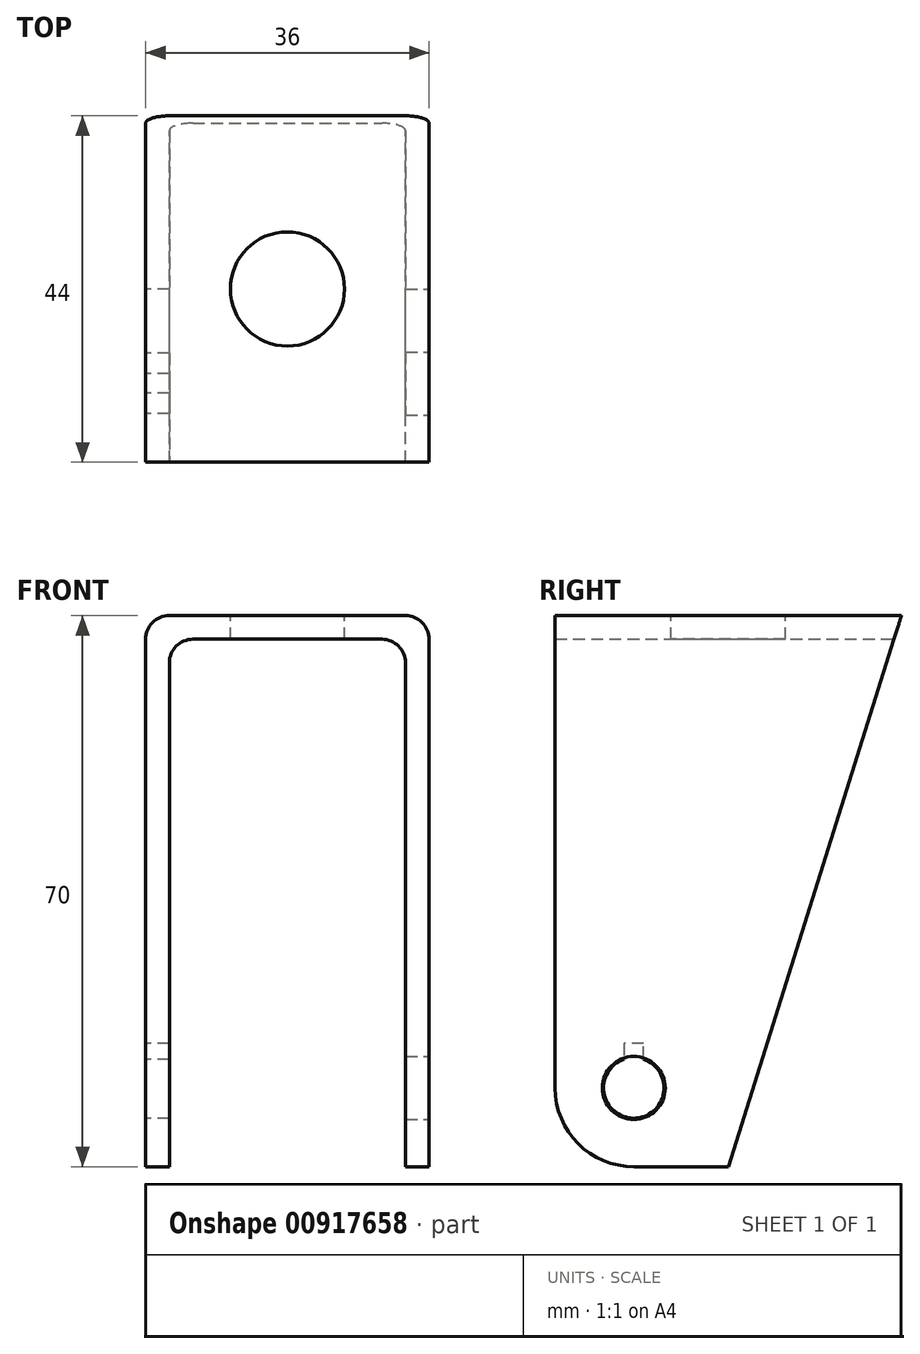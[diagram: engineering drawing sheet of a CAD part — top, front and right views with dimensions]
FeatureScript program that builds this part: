
annotation { "Feature Type Name" : "Feature", "Feature Type Description" : "" }
export const myFeature = defineFeature(function(context is Context, id is Id, definition is map)
    precondition{}
    {
        {
            var Q0;
            Q0=qCreatedBy(makeId("Front.planeOp"),FACE);
            var sketch = newSketch(context, id + "F0", { "sketchPlane" : qUnion([Q0])});
            skLineSegment(sketch, "E0", {"start": v(0, 0) * mm, "end": v(0, 70) * mm});
            skLineSegment(sketch, "E1", {"start": v(0, 70) * mm, "end": v(36, 70) * mm});
            skLineSegment(sketch, "E2", {"start": v(36, 70) * mm, "end": v(36, 0) * mm});
            skLineSegment(sketch, "E3", {"start": v(3, 0) * mm, "end": v(3, 67) * mm});
            skLineSegment(sketch, "E4", {"start": v(3, 67) * mm, "end": v(33, 67) * mm});
            skLineSegment(sketch, "E5", {"start": v(33, 67) * mm, "end": v(33, 0) * mm});
            skLineSegment(sketch, "E6", {"start": v(0, 0) * mm, "end": v(3, 0) * mm});
            skLineSegment(sketch, "E7", {"start": v(33, 0) * mm, "end": v(36, 0) * mm});
            skSolve(sketch);
        }
        {
            var Q0;
            Q0 = qSketchRegion(id + "F0", true);
            extrude(context, id + "F1", {"entities" : qUnion([Q0]), "depth" : 44 * mm, "offsetDistance" : 25 * mm});
        }
        {
            var Q0;
            Q0=makeQuery(id+"F1.opExtrude","SWEPT_FACE",FACE,{"disambiguationData":[OSD([sQuery(id+"F0.wireOp",EDGE,"E2")])]});
            var sketch = newSketch(context, id + "F2", { "sketchPlane" : qUnion([Q0])});
            skCircle(sketch, "E8", {"center": v(-34, 10) * mm, "radius": 4 * mm});
            skLineSegment(sketch, "E9", {"start": v(0, 70) * mm, "end": v(-22, 0) * mm});
            skSolve(sketch);
        }
        {
            var Q0;
            Q0=makeQuery(id+"F2.imprint","IMPRINT",FACE,{"disambiguationData":[TD([[makeQuery(id+"F2.imprint","IMPRINT",EDGE,{"derivedFrom":sQuery(id+"F2.wireOp",EDGE,"E8")}),1.0]])]});
            var Q1;
            {var subQ0=sQuery(id+"F2.wireOp",EDGE,"E9");Q1=makeQuery(id+"F2.imprint","IMPRINT",FACE,{"disambiguationData":[TD([[makeQuery(id+"F2.imprint","IMPRINT",EDGE,{"derivedFrom":subQ0}),1.0]])]});}
            extrude(context, id + "F3", {"entities" : qUnion([Q0, Q1]), "operationType" : NewBodyOperationType.REMOVE, "oppositeDirection" : true, "depth" : 25 * mm, "offsetDistance" : 25 * mm});
        }
        {
            var Q0;
            Q0=makeQuery(id+"F1.opExtrude","SWEPT_FACE",FACE,{"disambiguationData":[OSD([sQuery(id+"F0.wireOp",EDGE,"E0")])]});
            var sketch = newSketch(context, id + "F4", { "sketchPlane" : qUnion([Q0])});
            skLineSegment(sketch, "E10", {"start": v(0, 70) * mm, "end": v(22, 0) * mm});
            skArc(sketch, "E11", {"start": v(32.75, 13.63) * mm, "mid": v(34, 6.16) * mm, "end": v(35.25, 13.63) * mm});
            skLineSegment(sketch, "E12", {"start": v(32.75, 13.63) * mm, "end": v(32.75, 15.63) * mm});
            skLineSegment(sketch, "E13", {"start": v(32.75, 15.63) * mm, "end": v(35.25, 15.63) * mm});
            skLineSegment(sketch, "E14", {"start": v(35.25, 15.63) * mm, "end": v(35.25, 13.63) * mm});
            skSolve(sketch);
        }
        {
            var Q0;
            {var subQ0=sQuery(id+"F4.wireOp",EDGE,"E10");Q0=makeQuery(id+"F4.imprint","IMPRINT",FACE,{"disambiguationData":[TD([[makeQuery(id+"F4.imprint","IMPRINT",EDGE,{"derivedFrom":subQ0}),-1.0]])]});}
            var Q1;
            Q1=makeQuery(id+"F4.imprint","IMPRINT",FACE,{"disambiguationData":[TD([[makeQuery(id+"F4.imprint","IMPRINT",EDGE,{"derivedFrom":sQuery(id+"F4.wireOp",EDGE,"E11")}),1.0]])]});
            extrude(context, id + "F5", {"entities" : qUnion([Q0, Q1]), "operationType" : NewBodyOperationType.REMOVE, "oppositeDirection" : true, "depth" : 25 * mm, "offsetDistance" : 25 * mm});
        }
        {
            var Q0;
            Q0=makeQuery(id+"F1.opExtrude","SWEPT_EDGE",EDGE,{"disambiguationData":[OSD([sQuery(id+"F0.wireOp",EDGE,"E4"),sQuery(id+"F0.wireOp",EDGE,"E5")])]});
            var Q1;
            Q1=makeQuery(id+"F1.opExtrude","SWEPT_EDGE",EDGE,{"disambiguationData":[OSD([sQuery(id+"F0.wireOp",EDGE,"E3"),sQuery(id+"F0.wireOp",EDGE,"E4")])]});
            var Q2;
            Q2=makeQuery(id+"F1.opExtrude","SWEPT_EDGE",EDGE,{"disambiguationData":[OSD([sQuery(id+"F0.wireOp",EDGE,"E1"),sQuery(id+"F0.wireOp",EDGE,"E2")])]});
            var Q3;
            Q3=makeQuery(id+"F1.opExtrude","SWEPT_EDGE",EDGE,{"disambiguationData":[OSD([sQuery(id+"F0.wireOp",EDGE,"E0"),sQuery(id+"F0.wireOp",EDGE,"E1")])]});
            fillet(context, id + "F6", {"entities" : qUnion([Q0, Q1, Q2, Q3]), "radius" : 3 * mm, "tangentPropagation" : true, "allowEdgeOverflow" : false});
        }
        {
            var Q0;
            Q0=makeQuery(id+"F5.boolean.opBoolean","COPY",EDGE,{"derivedFrom":makeQuery(id+"F5.opExtrude","SWEPT_EDGE",EDGE,{"disambiguationData":[OSD([sQuery(id+"F0.wireOp",EDGE,"E0"),sQuery(id+"F0.wireOp",EDGE,"E6"),sQuery(id+"F4.wireOp",EDGE,"E10")])]})});
            var Q1;
            Q1=makeQuery(id+"F1.opExtrude","CAP_EDGE",EDGE,{"disambiguationData":[OSD([sQuery(id+"F0.wireOp",EDGE,"E6")])],"isStart":false});
            var Q2;
            Q2=makeQuery(id+"F1.opExtrude","CAP_EDGE",EDGE,{"disambiguationData":[OSD([sQuery(id+"F0.wireOp",EDGE,"E7")])],"isStart":false});
            var Q3;
            Q3=makeQuery(id+"F3.boolean.opBoolean","COPY",EDGE,{"derivedFrom":makeQuery(id+"F3.opExtrude","SWEPT_EDGE",EDGE,{"disambiguationData":[OSD([sQuery(id+"F0.wireOp",EDGE,"E2"),sQuery(id+"F0.wireOp",EDGE,"E7"),sQuery(id+"F2.wireOp",EDGE,"E9")])]})});
            fillet(context, id + "F7", {"entities" : qUnion([Q0, Q1, Q2, Q3]), "radius" : 10 * mm, "tangentPropagation" : true, "allowEdgeOverflow" : false});
        }
        {
            var Q0;
            Q0=makeQuery(id+"F1.opExtrude","SWEPT_FACE",FACE,{"disambiguationData":[OSD([sQuery(id+"F0.wireOp",EDGE,"E1")])]});
            var sketch = newSketch(context, id + "F8", { "sketchPlane" : qUnion([Q0])});
            skCircle(sketch, "E15", {"center": v(18, -22) * mm, "radius": 7.25 * mm});
            skSolve(sketch);
        }
        {
            var Q0;
            Q0=makeQuery(id+"F8.imprint","IMPRINT",FACE,{"disambiguationData":[TD([[makeQuery(id+"F8.imprint","IMPRINT",EDGE,{"derivedFrom":sQuery(id+"F8.wireOp",EDGE,"E15")}),1.0]])]});
            extrude(context, id + "F9", {"entities" : qUnion([Q0]), "operationType" : NewBodyOperationType.REMOVE, "oppositeDirection" : true, "depth" : 25 * mm, "offsetDistance" : 25 * mm});
        }
    });
